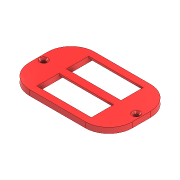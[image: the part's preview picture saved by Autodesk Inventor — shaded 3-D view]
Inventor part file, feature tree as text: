
AUTODESK INVENTOR PART (.ipt)
format: ipt  version: 2021 (Build 250183000, 183)  size: 128,512 bytes
history: native  units: mm
features: sketch x2, extrude x1, chamfer x1, hole x1, fillet x1
ambient origin geometry x8: Origin, YZ Plane, XZ Plane, XY Plane, X Axis, Y Axis, Z Axis, Center Point
bodies: Volumenkörper1 (feature_tree)
feature tree (6):
  extrude  "Extrusion1"  Depth=12.3mm
  chamfer  "Fase1"  Distance=12.3mm
  hole  "Bohrung1"  [1 undecoded]
  fillet  "Rundung1"  Radius=2.05mm
  sketch  "Skizze1"  dims[d0=30.2mm d1=12.3mm]
  sketch  "Skizze2"  dims[d2=30.2mm d3=12.3mm d5=4.1mm d6=2.05mm d7=56.9mm d8=36.0mm d9=3.0mm d10=0.0mm d11=2.0mm d12=2.0mm d13=45.0deg d14=51.3mm d15=2.4mm d16=6.0mm d17=4.4mm d18=2.0mm d19=90.0deg d20=8.0mm d21=20.594885mm d22=13.0mm]
note: 1 required parameter value undecoded (feature->parameter linkage not recoverable at this tier; creation-order binding heuristic only, values carry confidence <= 0.55)
